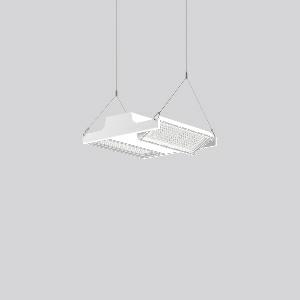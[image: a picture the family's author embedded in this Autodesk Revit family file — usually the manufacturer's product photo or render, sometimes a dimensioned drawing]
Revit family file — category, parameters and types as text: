
# Revit family: light_case_921680_002_1_76_cb47
name_source: partatom
category: Lighting Fixtures
units: mm (PartAtom-declared; Revit-internal decimal feet)

## family parameters
Cut with Voids When Loaded = No
Host = Face
Light Source = No
Part Type = Normal
Room Calculation Point = No
Round Connector Dimension = Use Diameter
Shared = No

## types (1)
- LIGHT CASE (1 x LED Modul 865, 8650 lm, 6500)
    Apparent Load = 117 VA
    CIE Flux Codes = 88 95 99 100 100
    Color Rendering = 80
    Color Temperature = 6500
    Default Elevation = 1800 mm
    Description = Series: LIGHT CASE
Flat highbay luminaire for chain or cable suspension with 2 LED modules that can be swivelled. Housing: die cast aluminium and sheet steel, powder-coated. Optimised thermal management thanks to special luminaire design. Self-cleaning heat sink for constant heat dissipation. Cover: plastic (polycarbonate, shockproof), with integrated four-row lens system. LED modules can be swivelled ± 30° for optimum illumination. Suitable for chain or steel cable suspension (to be provided on site). With 5-pin connection terminal (1.5 m). With integrated movement sensor and light sensor for daylight detection on request. Ball impact proof in accordance with DIN 18032-03 (except steel cable suspension). Luminaire with limited surface temperature in accordance with EN 60598-2-24 for use in environments in which a deposit of conductive dust on the luminaire can be expected. 
Colour: white
Length: 406 mm
Width: 397 mm
Height: 110 mm
Lamp: LED
Socket: without socket
Colour temperature: 6500K
Colour rendering index (CRI): 80
System power: 117 W
Rated luminous flux: 17300 lm
Luminous efficiency: 148 lm/W
Control gear: Converter, dimmable, DALI
Protection class: I
Type of protection: IP 65
    Height = 110 mm
    Lamp = 1 x LED Modul 865
    Lamp Light Flux = 8650 lm
    Lamp count = 1
    Length = 406 mm
    Lifetime = 50000 h
    Luminous efficacy = 148 lm/W
    Manufacturer = RZB
    ModVariant = No
    Model = 921680.002.1.76
    Mounting Place = Ceiling
    Mounting Type = Pendant
    Number of Poles = 1
    OnlyDefault = Yes
    Power Factor = 1
    Product Name = LIGHT CASE
    Product group = Pendant commercial luminaires
    ProductGroupID = 903
    Protection Class = Protection class I
    Protection Degree = IP 65
    RLX_Detail_Level = 1
    RLX_Emergency_Light_Flux = 0 lm
    RLX_Emergency_Type = 0
    RLX_Emergency_Type_DB = No
    RlxData = <blob elided: 25825 chars, md5=8d6f875b>
    Socket = socket
    Standby Power = 0 W
    System Light Flux = 17300 lm
    System Power = 117 W
    Type Comments = Product without accessories
    Type Image = 921517.002.76.jpg
    URL = http://relux.com
    VarID = ---
    Voltage = 230 V
    Voltage Range = 220-240 V
    Weight = 0.00 kg
    Width = 397 mm

## geometry (parser evidence)
native form markers: Blend x4, Sweep x19
no freeform markers — native parametric forms only
